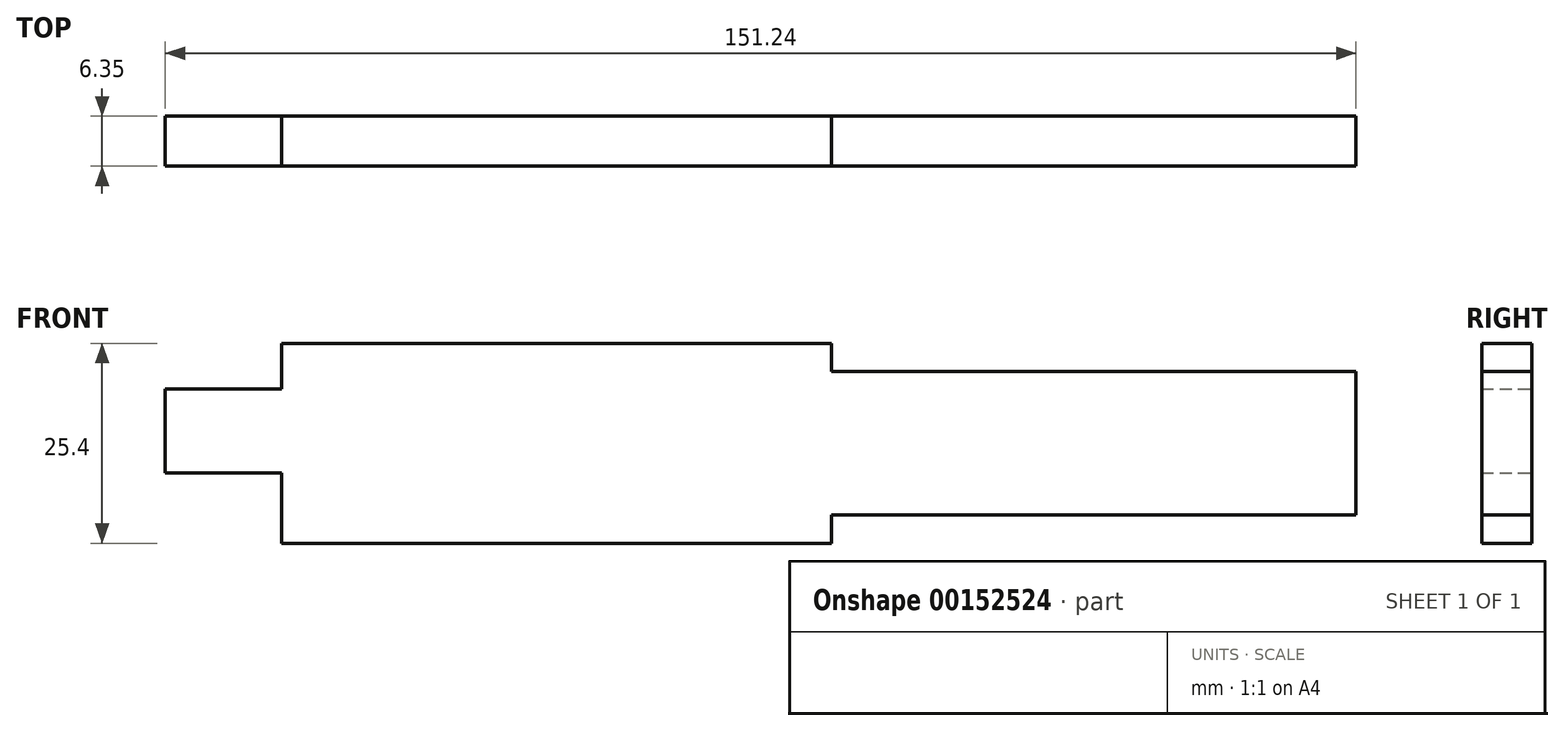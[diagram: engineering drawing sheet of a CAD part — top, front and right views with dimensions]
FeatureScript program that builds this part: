
annotation { "Feature Type Name" : "Feature", "Feature Type Description" : "" }
export const myFeature = defineFeature(function(context is Context, id is Id, definition is map)
    precondition{}
    {
        {
            var Q0;
            Q0=qCreatedBy(makeId("Front.planeOp"),FACE);
            var sketch = newSketch(context, id + "F0", { "sketchPlane" : qUnion([Q0])});
            skLineSegment(sketch, "E0.bottom", {"start": v(34.93, -12.7) * mm, "end": v(-34.93, -12.7) * mm});
            skLineSegment(sketch, "E0.top", {"start": v(34.93, 12.7) * mm, "end": v(-34.93, 12.7) * mm});
            skLineSegment(sketch, "E0.left", {"start": v(34.93, -12.7) * mm, "end": v(34.93, 12.7) * mm});
            skLineSegment(sketch, "E0.right", {"start": v(-34.93, -12.7) * mm, "end": v(-34.93, 12.7) * mm});
            skPoint(sketch, "E0.middle", {"position": v(0, 0) * mm});
            skSolve(sketch);
        }
        {
            var Q0;
            Q0 = qSketchRegion(id + "F0", true);
            extrude(context, id + "F1", {"entities" : qUnion([Q0]), "depth" : 6.35 * mm});
        }
        {
            var Q0;
            Q0=qCreatedBy(makeId("Front.planeOp"),FACE);
            var sketch = newSketch(context, id + "F2", { "sketchPlane" : qUnion([Q0])});
            skLineSegment(sketch, "E1.bottom", {"start": v(-49.71, -3.77) * mm, "end": v(-34.61, -3.77) * mm});
            skLineSegment(sketch, "E1.top", {"start": v(-49.71, 6.9) * mm, "end": v(-34.61, 6.9) * mm});
            skLineSegment(sketch, "E1.left", {"start": v(-49.71, -3.77) * mm, "end": v(-49.71, 6.9) * mm});
            skLineSegment(sketch, "E1.right", {"start": v(-34.61, -3.77) * mm, "end": v(-34.61, 6.9) * mm});
            skPoint(sketch, "E1.middle", {"position": v(-42.16, 1.57) * mm});
            skLineSegment(sketch, "E2.bottom", {"start": v(101.53, -9.12) * mm, "end": v(-12.77, -9.12) * mm});
            skLineSegment(sketch, "E2.top", {"start": v(101.53, 9.12) * mm, "end": v(-12.77, 9.12) * mm});
            skLineSegment(sketch, "E2.left", {"start": v(101.53, -9.12) * mm, "end": v(101.53, 9.12) * mm});
            skLineSegment(sketch, "E2.right", {"start": v(-12.77, -9.12) * mm, "end": v(-12.77, 9.12) * mm});
            skPoint(sketch, "E2.middle", {"position": v(44.38, 0) * mm});
            skSolve(sketch);
        }
        {
            var Q0;
            Q0 = qSketchRegion(id + "F2", true);
            extrude(context, id + "F3", {"entities" : qUnion([Q0]), "operationType" : NewBodyOperationType.ADD, "depth" : 6.35 * mm});
        }
    });
